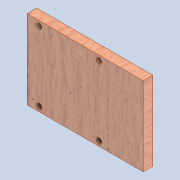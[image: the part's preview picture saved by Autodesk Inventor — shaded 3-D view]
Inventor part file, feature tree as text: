
AUTODESK INVENTOR PART (.ipt)
format: ipt  version: 2020 (Build 240168000, 168)  size: 177,664 bytes
history: native  units: mm
features: sketch x2, extrude x1, hole x1, pattern_linear x1
ambient origin geometry x8: Origin, YZ Plane, XZ Plane, XY Plane, X Axis, Y Axis, Z Axis, Center Point
bodies: Solid1 (feature_tree)
feature tree (5):
  extrude  "Extrusion1"  Depth=66.0mm
  hole  "Hole1"  [1 undecoded]
  pattern_linear  "Rectangular Pattern1"  Spacing1=4.0mm  [1 undecoded]
  sketch  "Sketch1"  dims[d0=97.0mm d1=66.0mm]
  sketch  "Sketch4"  dims[d2=8.0mm d3=0.0mm d19=10.0mm d20=4.0mm d21=4.0mm d22=4.5mm d23=6.0mm d24=4.0mm d25=2.0mm d26=90.0deg d27=8.0mm d28=20.594885mm d29=20.0mm d31=50.0mm]
note: 2 required parameter values undecoded (feature->parameter linkage not recoverable at this tier; creation-order binding heuristic only, values carry confidence <= 0.55)
